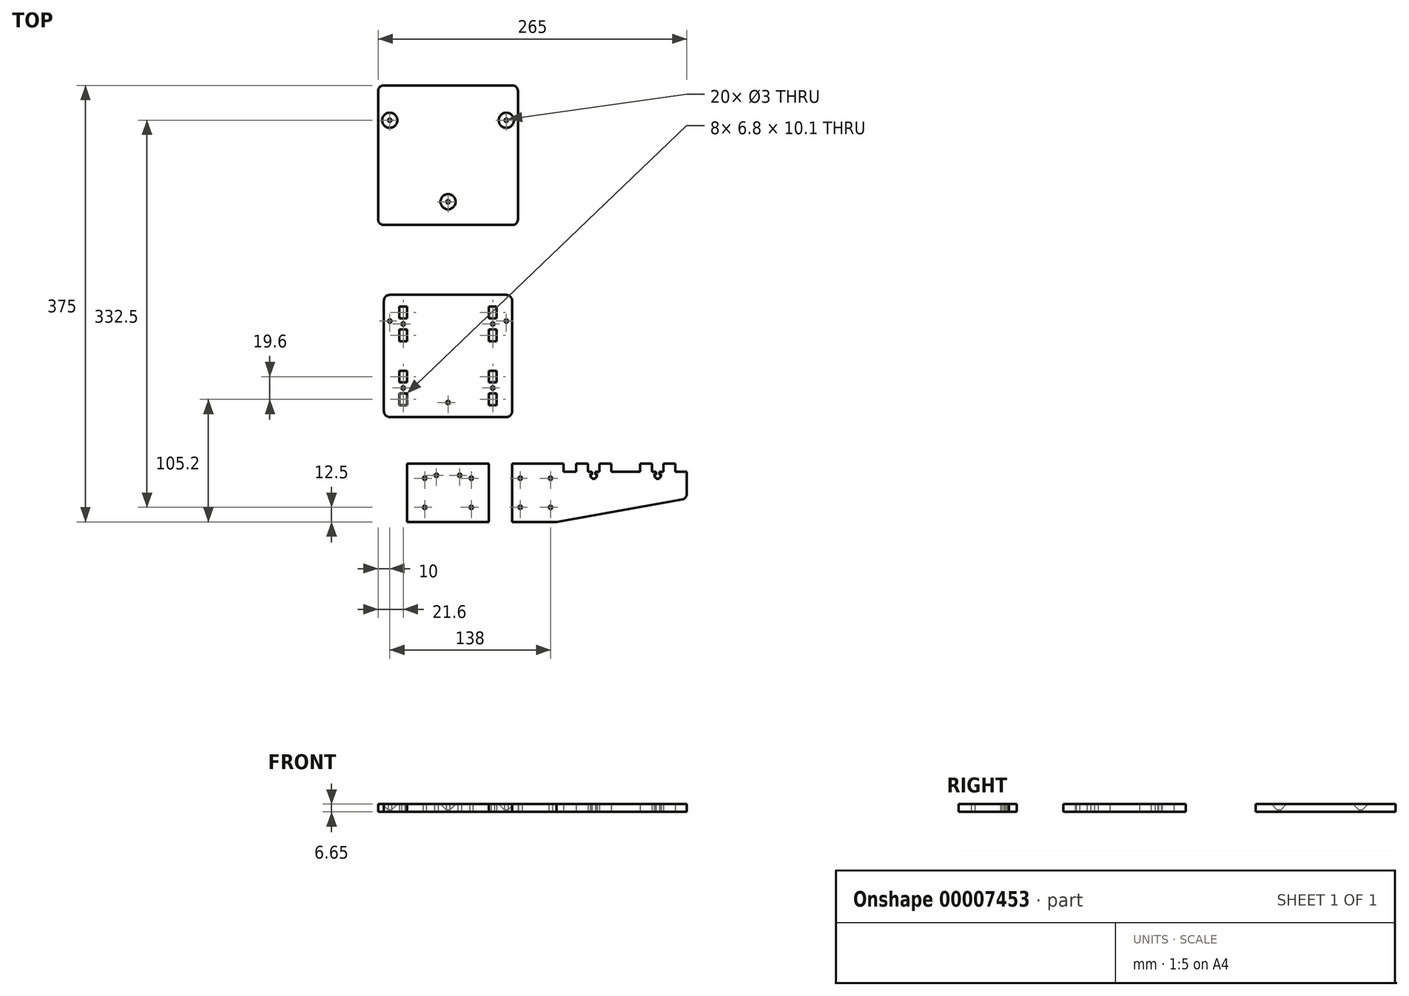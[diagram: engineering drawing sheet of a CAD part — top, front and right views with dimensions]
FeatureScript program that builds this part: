
annotation { "Feature Type Name" : "Feature", "Feature Type Description" : "" }
export const myFeature = defineFeature(function(context is Context, id is Id, definition is map)
    precondition{}
    {
        {
            var Q0;
            Q0=qCreatedBy(makeId("Top.planeOp"),FACE);
            var sketch = newSketch(context, id + "F0", { "sketchPlane" : qUnion([Q0])});
            skLineSegment(sketch, "E0", {"start": v(10, 75) * mm, "end": v(10, 25) * mm});
            skLineSegment(sketch, "E1", {"start": v(10, 25) * mm, "end": v(48, 25) * mm});
            skLineSegment(sketch, "E2", {"start": v(160, 45) * mm, "end": v(160, 75) * mm, "construction": true});
            skLineSegment(sketch, "E3", {"start": v(160, 75) * mm, "end": v(10, 75) * mm, "construction": true});
            skLineSegment(sketch, "E4.bottom", {"start": v(17, 62.5) * mm, "end": v(43, 62.5) * mm, "construction": true});
            skLineSegment(sketch, "E4.top", {"start": v(17, 37.5) * mm, "end": v(43, 37.5) * mm, "construction": true});
            skLineSegment(sketch, "E4.left", {"start": v(17, 62.5) * mm, "end": v(17, 37.5) * mm, "construction": true});
            skLineSegment(sketch, "E4.right", {"start": v(43, 62.5) * mm, "end": v(43, 37.5) * mm, "construction": true});
            skPoint(sketch, "E5", {"position": v(30, 62.5) * mm});
            skCircle(sketch, "E6", {"center": v(17, 62.5) * mm, "radius": 1.5 * mm});
            skCircle(sketch, "E7", {"center": v(43, 62.5) * mm, "radius": 1.5 * mm});
            skCircle(sketch, "E8", {"center": v(43, 37.5) * mm, "radius": 1.5 * mm});
            skCircle(sketch, "E9", {"center": v(17, 37.5) * mm, "radius": 1.5 * mm});
            skLineSegment(sketch, "E10", {"start": v(10, 75) * mm, "end": v(-10, 75) * mm, "construction": true});
            skLineSegment(sketch, "E11", {"start": v(10, 25) * mm, "end": v(-10, 25) * mm, "construction": true});
            skLineSegment(sketch, "E12", {"start": v(-10, 25) * mm, "end": v(-10, 75) * mm});
            skLineSegment(sketch, "E13", {"start": v(-10, 75) * mm, "end": v(-80, 75) * mm});
            skLineSegment(sketch, "E14", {"start": v(-80, 75) * mm, "end": v(-80, 25) * mm});
            skLineSegment(sketch, "E15", {"start": v(-80, 25) * mm, "end": v(-10, 25) * mm});
            skLineSegment(sketch, "E16", {"start": v(-25, 62.5) * mm, "end": v(-25, 37.5) * mm, "construction": true});
            skLineSegment(sketch, "E17", {"start": v(-45, 75) * mm, "end": v(-45, 25) * mm, "construction": true});
            skCircle(sketch, "E18", {"center": v(-25, 37.5) * mm, "radius": 1.5 * mm});
            skCircle(sketch, "E19", {"center": v(-25, 62.5) * mm, "radius": 1.5 * mm});
            skLineSegment(sketch, "E20", {"start": v(-25, 62.5) * mm, "end": v(17, 62.5) * mm, "construction": true});
            skLineSegment(sketch, "E21", {"start": v(-25, 37.5) * mm, "end": v(17, 37.5) * mm, "construction": true});
            skCircle(sketch, "E22.0.MirrorC", {"center": v(-65, 62.5) * mm, "radius": 1.5 * mm});
            skCircle(sketch, "E22.1.MirrorC", {"center": v(-65, 37.5) * mm, "radius": 1.5 * mm});
            skLineSegment(sketch, "E23", {"start": v(84.26, 170.76) * mm, "end": v(95.69, 170.76) * mm});
            skLineSegment(sketch, "E24", {"start": v(95.69, 170.76) * mm, "end": v(95.69, 177.56) * mm});
            skLineSegment(sketch, "E25", {"start": v(95.69, 177.56) * mm, "end": v(105.69, 177.56) * mm});
            skLineSegment(sketch, "E26", {"start": v(105.69, 177.56) * mm, "end": v(105.69, 170.76) * mm});
            skLineSegment(sketch, "E27", {"start": v(105.69, 170.76) * mm, "end": v(109.19, 170.76) * mm});
            skLineSegment(sketch, "E28", {"start": v(109.19, 170.76) * mm, "end": v(109.19, 168.21) * mm});
            skLineSegment(sketch, "E29", {"start": v(109.19, 168.21) * mm, "end": v(107.94, 168.21) * mm});
            skLineSegment(sketch, "E30", {"start": v(107.94, 168.21) * mm, "end": v(107.94, 165.91) * mm});
            skLineSegment(sketch, "E31", {"start": v(107.94, 165.91) * mm, "end": v(109.19, 165.91) * mm});
            skLineSegment(sketch, "E32", {"start": v(109.19, 165.91) * mm, "end": v(109.19, 164.56) * mm});
            skLineSegment(sketch, "E33", {"start": v(109.19, 164.56) * mm, "end": v(112.19, 164.56) * mm});
            skLineSegment(sketch, "E34", {"start": v(112.19, 164.56) * mm, "end": v(112.19, 165.91) * mm});
            skLineSegment(sketch, "E35", {"start": v(112.19, 165.91) * mm, "end": v(113.44, 165.91) * mm});
            skLineSegment(sketch, "E36", {"start": v(113.44, 165.91) * mm, "end": v(113.44, 168.21) * mm});
            skLineSegment(sketch, "E37", {"start": v(113.44, 168.21) * mm, "end": v(112.19, 168.21) * mm});
            skLineSegment(sketch, "E38", {"start": v(112.19, 168.21) * mm, "end": v(112.19, 170.76) * mm});
            skLineSegment(sketch, "E39", {"start": v(112.19, 170.76) * mm, "end": v(115.69, 170.76) * mm});
            skLineSegment(sketch, "E40", {"start": v(115.69, 170.76) * mm, "end": v(115.69, 177.56) * mm});
            skLineSegment(sketch, "E41", {"start": v(115.69, 177.56) * mm, "end": v(125.69, 177.56) * mm});
            skLineSegment(sketch, "E42", {"start": v(125.69, 177.56) * mm, "end": v(125.69, 170.76) * mm});
            skLineSegment(sketch, "E43", {"start": v(125.69, 170.76) * mm, "end": v(133.4, 170.76) * mm});
            skLineSegment(sketch, "E44", {"start": v(-45, 65) * mm, "end": v(-35, 65) * mm, "construction": true});
            skCircle(sketch, "E45", {"center": v(-35, 65) * mm, "radius": 1.5 * mm});
            skCircle(sketch, "E46.0.MirrorC", {"center": v(-55, 65) * mm, "radius": 1.5 * mm});
            skLineSegment(sketch, "E47", {"start": v(-10, 75) * mm, "end": v(-10, 115) * mm, "construction": true});
            skLineSegment(sketch, "E48", {"start": v(-10, 115) * mm, "end": v(5, 115) * mm});
            skLineSegment(sketch, "E49", {"start": v(10, 120) * mm, "end": v(10, 215) * mm});
            skLineSegment(sketch, "E50", {"start": v(5, 220) * mm, "end": v(-10, 220) * mm});
            skLineSegment(sketch, "E51", {"start": v(-10, 115) * mm, "end": v(-45, 115) * mm});
            skLineSegment(sketch, "E52", {"start": v(-45, 115) * mm, "end": v(-45, 220) * mm, "construction": true});
            skLineSegment(sketch, "E53", {"start": v(-45, 220) * mm, "end": v(-10, 220) * mm});
            skLineSegment(sketch, "E54", {"start": v(-45, 115) * mm, "end": v(-45, 75) * mm, "construction": true});
            skLineSegment(sketch, "E55", {"start": v(105.69, 177.56) * mm, "end": v(115.69, 177.56) * mm, "construction": true});
            skLineSegment(sketch, "E56", {"start": v(109.19, 170.76) * mm, "end": v(112.19, 170.76) * mm, "construction": true});
            skLineSegment(sketch, "E57", {"start": v(109.19, 168.21) * mm, "end": v(112.19, 168.21) * mm, "construction": true});
            skLineSegment(sketch, "E58", {"start": v(109.19, 165.91) * mm, "end": v(112.19, 165.91) * mm, "construction": true});
            skLineSegment(sketch, "E59", {"start": v(109.19, 168.21) * mm, "end": v(109.19, 165.91) * mm, "construction": true});
            skLineSegment(sketch, "E60", {"start": v(112.19, 165.91) * mm, "end": v(112.19, 168.21) * mm, "construction": true});
            skLineSegment(sketch, "E61", {"start": v(110.69, 170.76) * mm, "end": v(110.69, 177.56) * mm, "construction": true});
            skCircle(sketch, "E62", {"center": v(107.94, 168.21) * mm, "radius": 0.25 * mm});
            skCircle(sketch, "E63", {"center": v(113.44, 168.21) * mm, "radius": 0.25 * mm});
            skLineSegment(sketch, "E64", {"start": v(95.69, 130.76) * mm, "end": v(125.39, 130.76) * mm, "construction": true});
            skLineSegment(sketch, "E65", {"start": v(125.39, 130.76) * mm, "end": v(125.39, 123.96) * mm});
            skLineSegment(sketch, "E66", {"start": v(125.39, 123.96) * mm, "end": v(95.69, 123.96) * mm, "construction": true});
            skLineSegment(sketch, "E67", {"start": v(95.69, 123.96) * mm, "end": v(95.69, 130.76) * mm});
            skLineSegment(sketch, "E68", {"start": v(95.69, 130.76) * mm, "end": v(105.79, 130.76) * mm});
            skLineSegment(sketch, "E69", {"start": v(105.79, 130.76) * mm, "end": v(105.79, 123.96) * mm});
            skLineSegment(sketch, "E70", {"start": v(105.79, 123.96) * mm, "end": v(95.69, 123.96) * mm});
            skLineSegment(sketch, "E71", {"start": v(125.39, 123.96) * mm, "end": v(115.29, 123.96) * mm});
            skLineSegment(sketch, "E72", {"start": v(115.29, 123.96) * mm, "end": v(115.29, 130.76) * mm});
            skLineSegment(sketch, "E73", {"start": v(115.29, 130.76) * mm, "end": v(125.39, 130.76) * mm});
            skLineSegment(sketch, "E74", {"start": v(110.54, 130.76) * mm, "end": v(110.54, 123.96) * mm, "construction": true});
            skCircle(sketch, "E75", {"center": v(110.54, 127.36) * mm, "radius": 1.5 * mm});
            skLineSegment(sketch, "E76", {"start": v(95.69, 170.76) * mm, "end": v(95.69, 130.76) * mm, "construction": true});
            skLineSegment(sketch, "E77", {"start": v(-10, 125.15) * mm, "end": v(-10, 154.85) * mm, "construction": true});
            skLineSegment(sketch, "E78", {"start": v(-10, 154.85) * mm, "end": v(-3.2, 154.85) * mm});
            skLineSegment(sketch, "E79", {"start": v(-3.2, 154.85) * mm, "end": v(-3.2, 125.15) * mm, "construction": true});
            skLineSegment(sketch, "E80", {"start": v(-3.2, 125.15) * mm, "end": v(-10, 125.15) * mm});
            skLineSegment(sketch, "E81", {"start": v(-10, 125.15) * mm, "end": v(-10, 135.25) * mm});
            skLineSegment(sketch, "E82", {"start": v(-10, 135.25) * mm, "end": v(-3.2, 135.25) * mm});
            skLineSegment(sketch, "E83", {"start": v(-3.2, 135.25) * mm, "end": v(-3.2, 125.15) * mm});
            skLineSegment(sketch, "E84", {"start": v(-3.2, 154.85) * mm, "end": v(-3.2, 144.75) * mm});
            skLineSegment(sketch, "E85", {"start": v(-3.2, 144.75) * mm, "end": v(-10, 144.75) * mm});
            skLineSegment(sketch, "E86", {"start": v(-10, 144.75) * mm, "end": v(-10, 154.85) * mm});
            skLineSegment(sketch, "E87", {"start": v(-10, 140) * mm, "end": v(-3.2, 140) * mm, "construction": true});
            skCircle(sketch, "E88", {"center": v(-6.6, 140) * mm, "radius": 1.5 * mm});
            skLineSegment(sketch, "E89", {"start": v(-10, 115) * mm, "end": v(-10, 220) * mm, "construction": true});
            skLineSegment(sketch, "E90.0.MirrorCS", {"start": v(-80, 115) * mm, "end": v(-45, 115) * mm});
            skLineSegment(sketch, "E90.1.MirrorCS", {"start": v(-80, 115) * mm, "end": v(-95, 115) * mm});
            skLineSegment(sketch, "E90.2.MirrorCS", {"start": v(-100, 120) * mm, "end": v(-100, 215) * mm});
            skLineSegment(sketch, "E90.3.MirrorCS", {"start": v(-95, 220) * mm, "end": v(-80, 220) * mm});
            skLineSegment(sketch, "E90.4.MirrorCS", {"start": v(-45, 220) * mm, "end": v(-80, 220) * mm});
            skLineSegment(sketch, "E91.0.1.0", {"start": v(-3.2, 190.25) * mm, "end": v(-3.2, 180.15) * mm});
            skLineSegment(sketch, "E91.0.1.1", {"start": v(-3.2, 180.15) * mm, "end": v(-10, 180.15) * mm});
            skLineSegment(sketch, "E91.0.1.2", {"start": v(-10, 180.15) * mm, "end": v(-10, 190.25) * mm});
            skLineSegment(sketch, "E91.0.1.3", {"start": v(-10, 190.25) * mm, "end": v(-3.2, 190.25) * mm});
            skLineSegment(sketch, "E91.0.1.4", {"start": v(-3.2, 209.85) * mm, "end": v(-3.2, 180.15) * mm, "construction": true});
            skLineSegment(sketch, "E91.0.1.5", {"start": v(-10, 195) * mm, "end": v(-3.2, 195) * mm, "construction": true});
            skCircle(sketch, "E91.0.1.6", {"center": v(-6.6, 195) * mm, "radius": 1.5 * mm});
            skLineSegment(sketch, "E91.0.1.7", {"start": v(-3.2, 199.75) * mm, "end": v(-10, 199.75) * mm});
            skLineSegment(sketch, "E91.0.1.8", {"start": v(-3.2, 209.85) * mm, "end": v(-3.2, 199.75) * mm});
            skLineSegment(sketch, "E91.0.1.9", {"start": v(-10, 199.75) * mm, "end": v(-10, 209.85) * mm});
            skLineSegment(sketch, "E91.0.1.10", {"start": v(-10, 209.85) * mm, "end": v(-3.2, 209.85) * mm});
            skLineSegment(sketch, "E91.0.1.11", {"start": v(-10, 180.15) * mm, "end": v(-10, 209.85) * mm, "construction": true});
            skLineSegment(sketch, "E91.direction1", {"start": v(-3.2, 125.15) * mm, "end": v(5.96, 125.15) * mm, "construction": true});
            skLineSegment(sketch, "E91.direction2", {"start": v(-3.2, 125.15) * mm, "end": v(-3.2, 180.15) * mm, "construction": true});
            skLineSegment(sketch, "E92", {"start": v(10, 75) * mm, "end": v(54, 75) * mm});
            skLineSegment(sketch, "E93", {"start": v(54, 75) * mm, "end": v(54, 68.2) * mm});
            skLineSegment(sketch, "E94", {"start": v(54, 68.2) * mm, "end": v(108.05, 68.2) * mm, "construction": true});
            skLineSegment(sketch, "E95", {"start": v(78.5, 68.2) * mm, "end": v(78.5, 62) * mm, "construction": true});
            skLineSegment(sketch, "E96", {"start": v(78.5, 62) * mm, "end": v(81.5, 62) * mm});
            skLineSegment(sketch, "E97", {"start": v(81.5, 62) * mm, "end": v(81.5, 68.2) * mm, "construction": true});
            skLineSegment(sketch, "E98", {"start": v(78.5, 65.65) * mm, "end": v(77.25, 65.65) * mm});
            skLineSegment(sketch, "E99", {"start": v(77.25, 65.65) * mm, "end": v(77.25, 63.35) * mm});
            skLineSegment(sketch, "E100", {"start": v(77.25, 63.35) * mm, "end": v(78.5, 63.35) * mm});
            skLineSegment(sketch, "E101", {"start": v(78.5, 63.35) * mm, "end": v(81.5, 63.35) * mm, "construction": true});
            skLineSegment(sketch, "E102", {"start": v(81.5, 63.35) * mm, "end": v(82.75, 63.35) * mm});
            skLineSegment(sketch, "E103", {"start": v(82.75, 63.35) * mm, "end": v(82.75, 65.65) * mm});
            skLineSegment(sketch, "E104", {"start": v(82.75, 65.65) * mm, "end": v(81.5, 65.65) * mm});
            skLineSegment(sketch, "E105", {"start": v(81.5, 65.65) * mm, "end": v(78.5, 65.65) * mm, "construction": true});
            skLineSegment(sketch, "E106", {"start": v(54, 68.2) * mm, "end": v(65, 68.2) * mm});
            skLineSegment(sketch, "E107", {"start": v(65, 68.2) * mm, "end": v(65, 75) * mm});
            skLineSegment(sketch, "E108", {"start": v(65, 75) * mm, "end": v(75, 75) * mm});
            skLineSegment(sketch, "E109", {"start": v(75, 75) * mm, "end": v(75, 68.2) * mm});
            skLineSegment(sketch, "E110", {"start": v(75, 68.2) * mm, "end": v(78.5, 68.2) * mm});
            skLineSegment(sketch, "E111", {"start": v(81.5, 68.2) * mm, "end": v(85, 68.2) * mm});
            skLineSegment(sketch, "E112", {"start": v(85, 68.2) * mm, "end": v(85, 75) * mm});
            skLineSegment(sketch, "E113", {"start": v(85, 75) * mm, "end": v(95, 75) * mm});
            skLineSegment(sketch, "E114", {"start": v(95, 75) * mm, "end": v(95, 68.2) * mm});
            skLineSegment(sketch, "E115", {"start": v(81.5, 68.2) * mm, "end": v(81.5, 65.65) * mm});
            skLineSegment(sketch, "E116", {"start": v(81.5, 63.35) * mm, "end": v(81.5, 62) * mm});
            skLineSegment(sketch, "E117", {"start": v(78.5, 63.35) * mm, "end": v(78.5, 62) * mm});
            skLineSegment(sketch, "E118", {"start": v(78.5, 65.65) * mm, "end": v(78.5, 68.2) * mm});
            skLineSegment(sketch, "E119", {"start": v(160, 68.2) * mm, "end": v(160, 49.19) * mm});
            skCircle(sketch, "E120", {"center": v(82.75, 65.65) * mm, "radius": 0.25 * mm});
            skCircle(sketch, "E121", {"center": v(77.25, 65.65) * mm, "radius": 0.25 * mm});
            skLineSegment(sketch, "E122.1.0.0", {"start": v(136.5, 68.2) * mm, "end": v(140, 68.2) * mm});
            skLineSegment(sketch, "E122.1.0.1", {"start": v(120, 75) * mm, "end": v(130, 75) * mm});
            skLineSegment(sketch, "E122.1.0.2", {"start": v(133.5, 65.65) * mm, "end": v(132.25, 65.65) * mm});
            skLineSegment(sketch, "E122.1.0.3", {"start": v(150, 75) * mm, "end": v(150, 68.2) * mm});
            skLineSegment(sketch, "E122.1.0.4", {"start": v(120, 68.2) * mm, "end": v(120, 75) * mm});
            skCircle(sketch, "E122.1.0.5", {"center": v(137.75, 65.65) * mm, "radius": 0.25 * mm});
            skLineSegment(sketch, "E122.1.0.6", {"start": v(136.5, 63.35) * mm, "end": v(137.75, 63.35) * mm});
            skLineSegment(sketch, "E122.1.0.7", {"start": v(133.5, 65.65) * mm, "end": v(133.5, 68.2) * mm});
            skLineSegment(sketch, "E122.1.0.8", {"start": v(130, 68.2) * mm, "end": v(133.5, 68.2) * mm});
            skLineSegment(sketch, "E122.1.0.9", {"start": v(130, 75) * mm, "end": v(130, 68.2) * mm});
            skCircle(sketch, "E122.1.0.10", {"center": v(132.25, 65.65) * mm, "radius": 0.25 * mm});
            skLineSegment(sketch, "E122.1.0.11", {"start": v(136.5, 63.35) * mm, "end": v(136.5, 62) * mm});
            skLineSegment(sketch, "E122.1.0.12", {"start": v(137.75, 65.65) * mm, "end": v(136.5, 65.65) * mm});
            skLineSegment(sketch, "E122.1.0.13", {"start": v(140, 75) * mm, "end": v(150, 75) * mm});
            skLineSegment(sketch, "E122.1.0.14", {"start": v(140, 68.2) * mm, "end": v(140, 75) * mm});
            skLineSegment(sketch, "E122.1.0.15", {"start": v(133.5, 62) * mm, "end": v(136.5, 62) * mm});
            skLineSegment(sketch, "E122.1.0.16", {"start": v(133.5, 63.35) * mm, "end": v(136.5, 63.35) * mm, "construction": true});
            skLineSegment(sketch, "E122.1.0.17", {"start": v(133.5, 63.35) * mm, "end": v(133.5, 62) * mm});
            skLineSegment(sketch, "E122.1.0.18", {"start": v(136.5, 68.2) * mm, "end": v(136.5, 65.65) * mm});
            skLineSegment(sketch, "E122.1.0.19", {"start": v(132.25, 65.65) * mm, "end": v(132.25, 63.35) * mm});
            skLineSegment(sketch, "E122.1.0.20", {"start": v(133.5, 68.2) * mm, "end": v(133.5, 62) * mm, "construction": true});
            skLineSegment(sketch, "E122.1.0.21", {"start": v(137.75, 63.35) * mm, "end": v(137.75, 65.65) * mm});
            skLineSegment(sketch, "E122.1.0.22", {"start": v(132.25, 63.35) * mm, "end": v(133.5, 63.35) * mm});
            skLineSegment(sketch, "E122.1.0.23", {"start": v(136.5, 62) * mm, "end": v(136.5, 68.2) * mm, "construction": true});
            skLineSegment(sketch, "E122.1.0.24", {"start": v(136.5, 65.65) * mm, "end": v(133.5, 65.65) * mm, "construction": true});
            skLineSegment(sketch, "E122.direction1", {"start": v(81.5, 68.2) * mm, "end": v(136.5, 68.2) * mm, "construction": true});
            skLineSegment(sketch, "E123", {"start": v(120, 68.2) * mm, "end": v(95, 68.2) * mm});
            skLineSegment(sketch, "E124", {"start": v(150, 68.2) * mm, "end": v(160, 68.2) * mm});
            skLineSegment(sketch, "E125", {"start": v(48, 25) * mm, "end": v(155.88, 44.26) * mm});
            skPoint(sketch, "E126.visualSharp", {"position": v(10, 220) * mm});
            skArc(sketch, "E126.filletArc", {"start": v(10, 215) * mm, "mid": v(8.54, 218.54) * mm, "end": v(5, 220) * mm});
            skPoint(sketch, "E127.visualSharp", {"position": v(10, 115) * mm});
            skArc(sketch, "E127.filletArc", {"start": v(5, 115) * mm, "mid": v(8.54, 116.46) * mm, "end": v(10, 120) * mm});
            skPoint(sketch, "E128.visualSharp", {"position": v(160, 45) * mm});
            skArc(sketch, "E128.filletArc", {"start": v(155.88, 44.26) * mm, "mid": v(158.83, 45.98) * mm, "end": v(160, 49.19) * mm});
            skPoint(sketch, "E129.visualSharp", {"position": v(-100, 115) * mm});
            skArc(sketch, "E129.filletArc", {"start": v(-100, 120) * mm, "mid": v(-98.54, 116.46) * mm, "end": v(-95, 115) * mm});
            skPoint(sketch, "E130.visualSharp", {"position": v(-100, 220) * mm});
            skArc(sketch, "E130.filletArc", {"start": v(-95, 220) * mm, "mid": v(-98.54, 218.54) * mm, "end": v(-100, 215) * mm});
            skLineSegment(sketch, "E131", {"start": v(-45, 167.5) * mm, "end": v(-26.23, 167.5) * mm, "construction": true});
            skCircle(sketch, "E132", {"center": v(-45, 127.5) * mm, "radius": 1.5 * mm});
            skCircle(sketch, "E133", {"center": v(5, 197.5) * mm, "radius": 1.5 * mm});
            skCircle(sketch, "E134.0.MirrorC", {"center": v(-95, 197.5) * mm, "radius": 1.5 * mm});
            skLineSegment(sketch, "E135", {"start": v(-45, 167.5) * mm, "end": v(-45, 197.5) * mm, "construction": true});
            skLineSegment(sketch, "E136", {"start": v(-45, 197.5) * mm, "end": v(5, 197.5) * mm, "construction": true});
            skLineSegment(sketch, "E137", {"start": v(-45, 167.5) * mm, "end": v(-45, 127.5) * mm, "construction": true});
            skLineSegment(sketch, "E138", {"start": v(-45, 220) * mm, "end": v(-45, 280) * mm, "construction": true});
            skLineSegment(sketch, "E139", {"start": v(-45, 280) * mm, "end": v(10, 280) * mm});
            skLineSegment(sketch, "E140", {"start": v(15, 285) * mm, "end": v(15, 395) * mm});
            skLineSegment(sketch, "E141", {"start": v(10, 400) * mm, "end": v(-45, 400) * mm});
            skLineSegment(sketch, "E142", {"start": v(-45, 400) * mm, "end": v(-45, 280) * mm, "construction": true});
            skLineSegment(sketch, "E143", {"start": v(-45, 340) * mm, "end": v(-45, 300) * mm, "construction": true});
            skLineSegment(sketch, "E144", {"start": v(-45, 340) * mm, "end": v(-45, 370) * mm, "construction": true});
            skLineSegment(sketch, "E145", {"start": v(-45, 370) * mm, "end": v(5, 370) * mm, "construction": true});
            skCircle(sketch, "E146", {"center": v(-45, 300) * mm, "radius": 1.5 * mm});
            skCircle(sketch, "E147", {"center": v(5, 370) * mm, "radius": 1.5 * mm});
            skPoint(sketch, "E148.visualSharp", {"position": v(15, 400) * mm});
            skArc(sketch, "E148.filletArc", {"start": v(15, 395) * mm, "mid": v(13.54, 398.54) * mm, "end": v(10, 400) * mm});
            skPoint(sketch, "E149.visualSharp", {"position": v(15, 280) * mm});
            skArc(sketch, "E149.filletArc", {"start": v(10, 280) * mm, "mid": v(13.54, 281.46) * mm, "end": v(15, 285) * mm});
            skCircle(sketch, "E150.0.MirrorC", {"center": v(-95, 370) * mm, "radius": 1.5 * mm});
            skLineSegment(sketch, "E150.1.MirrorCS", {"start": v(-100, 400) * mm, "end": v(-45, 400) * mm});
            skArc(sketch, "E150.2.MirrorCS", {"start": v(-105, 395) * mm, "mid": v(-103.54, 398.54) * mm, "end": v(-100, 400) * mm});
            skLineSegment(sketch, "E150.3.MirrorCS", {"start": v(-105, 285) * mm, "end": v(-105, 395) * mm});
            skLineSegment(sketch, "E150.4.MirrorCS", {"start": v(-45, 280) * mm, "end": v(-100, 280) * mm});
            skArc(sketch, "E150.5.MirrorCS", {"start": v(-100, 280) * mm, "mid": v(-103.54, 281.46) * mm, "end": v(-105, 285) * mm});
            skPoint(sketch, "E151", {"position": v(107.94, 167.06) * mm});
            skLineSegment(sketch, "E152.0.MirrorCS", {"start": v(-80, 180.15) * mm, "end": v(-80, 190.25) * mm});
            skLineSegment(sketch, "E152.1.MirrorCS", {"start": v(-86.8, 180.15) * mm, "end": v(-80, 180.15) * mm});
            skLineSegment(sketch, "E152.2.MirrorCS", {"start": v(-86.8, 190.25) * mm, "end": v(-86.8, 180.15) * mm});
            skLineSegment(sketch, "E152.3.MirrorCS", {"start": v(-80, 190.25) * mm, "end": v(-86.8, 190.25) * mm});
            skCircle(sketch, "E152.4.MirrorC", {"center": v(-83.4, 195) * mm, "radius": 1.5 * mm});
            skLineSegment(sketch, "E152.5.MirrorCS", {"start": v(-80, 199.75) * mm, "end": v(-80, 209.85) * mm});
            skLineSegment(sketch, "E152.6.MirrorCS", {"start": v(-86.8, 199.75) * mm, "end": v(-80, 199.75) * mm});
            skLineSegment(sketch, "E152.7.MirrorCS", {"start": v(-86.8, 209.85) * mm, "end": v(-86.8, 199.75) * mm});
            skLineSegment(sketch, "E152.8.MirrorCS", {"start": v(-80, 209.85) * mm, "end": v(-86.8, 209.85) * mm});
            skLineSegment(sketch, "E152.9.MirrorCS", {"start": v(-80, 144.75) * mm, "end": v(-80, 154.85) * mm});
            skLineSegment(sketch, "E152.10.MirrorCS", {"start": v(-80, 154.85) * mm, "end": v(-86.8, 154.85) * mm});
            skLineSegment(sketch, "E152.11.MirrorCS", {"start": v(-86.8, 154.85) * mm, "end": v(-86.8, 144.75) * mm});
            skLineSegment(sketch, "E152.12.MirrorCS", {"start": v(-86.8, 144.75) * mm, "end": v(-80, 144.75) * mm});
            skCircle(sketch, "E152.13.MirrorC", {"center": v(-83.4, 140) * mm, "radius": 1.5 * mm});
            skLineSegment(sketch, "E152.14.MirrorCS", {"start": v(-86.8, 125.15) * mm, "end": v(-80, 125.15) * mm});
            skLineSegment(sketch, "E152.15.MirrorCS", {"start": v(-80, 125.15) * mm, "end": v(-80, 135.25) * mm});
            skLineSegment(sketch, "E152.16.MirrorCS", {"start": v(-86.8, 135.25) * mm, "end": v(-86.8, 125.15) * mm});
            skLineSegment(sketch, "E152.17.MirrorCS", {"start": v(-80, 135.25) * mm, "end": v(-86.8, 135.25) * mm});
            skSolve(sketch);
        }
        {
            var Q0;
            Q0=makeQuery(id+"F0.imprint","IMPRINT",FACE,{"disambiguationData":[TD([[makeQuery(id+"F0.imprint","IMPRINT",EDGE,{"derivedFrom":sQuery(id+"F0.wireOp",EDGE,"E0")}),1.0]])]});
            extrude(context, id + "F1", {"entities" : qUnion([Q0]), "depth" : 6.65 * mm});
        }
        {
            var Q0;
            Q0=makeQuery(id+"F0.imprint","IMPRINT",FACE,{"disambiguationData":[TD([[makeQuery(id+"F0.imprint","IMPRINT",EDGE,{"derivedFrom":sQuery(id+"F0.wireOp",EDGE,"E12")}),1.0]])]});
            extrude(context, id + "F2", {"entities" : qUnion([Q0]), "depth" : 6.65 * mm});
        }
        {
            var Q0;
            Q0=makeQuery(id+"F0.imprint","IMPRINT",FACE,{"disambiguationData":[TD([[makeQuery(id+"F0.imprint","IMPRINT",EDGE,{"derivedFrom":sQuery(id+"F0.wireOp",EDGE,"E48")}),1.0]])]});
            extrude(context, id + "F3", {"entities" : qUnion([Q0]), "depth" : 6.65 * mm});
        }
        {
            var Q0;
            Q0=makeQuery(id+"F0.imprint","IMPRINT",FACE,{"disambiguationData":[TD([[makeQuery(id+"F0.imprint","IMPRINT",EDGE,{"derivedFrom":sQuery(id+"F0.wireOp",EDGE,"E139")}),1.0]])]});
            extrude(context, id + "F4", {"entities" : qUnion([Q0]), "depth" : 6.65 * mm});
        }
        {
            var Q0;
            Q0=makeQuery(id+"F4.opExtrude","CAP_EDGE",EDGE,{"disambiguationData":[OSD([sQuery(id+"F0.wireOp",EDGE,"E146")])],"isStart":false});
            var Q1;
            Q1=makeQuery(id+"F4.opExtrude","CAP_EDGE",EDGE,{"disambiguationData":[OSD([sQuery(id+"F0.wireOp",EDGE,"E147")])],"isStart":false});
            var Q2;
            Q2=makeQuery(id+"F4.opExtrude","CAP_EDGE",EDGE,{"disambiguationData":[OSD([sQuery(id+"F0.wireOp",EDGE,"E150.0.MirrorC")])],"isStart":false});
            chamfer(context, id + "F5", {"entities" : qUnion([Q0, Q1, Q2]), "width" : 5 * mm, "tangentPropagation" : true});
        }
    });
